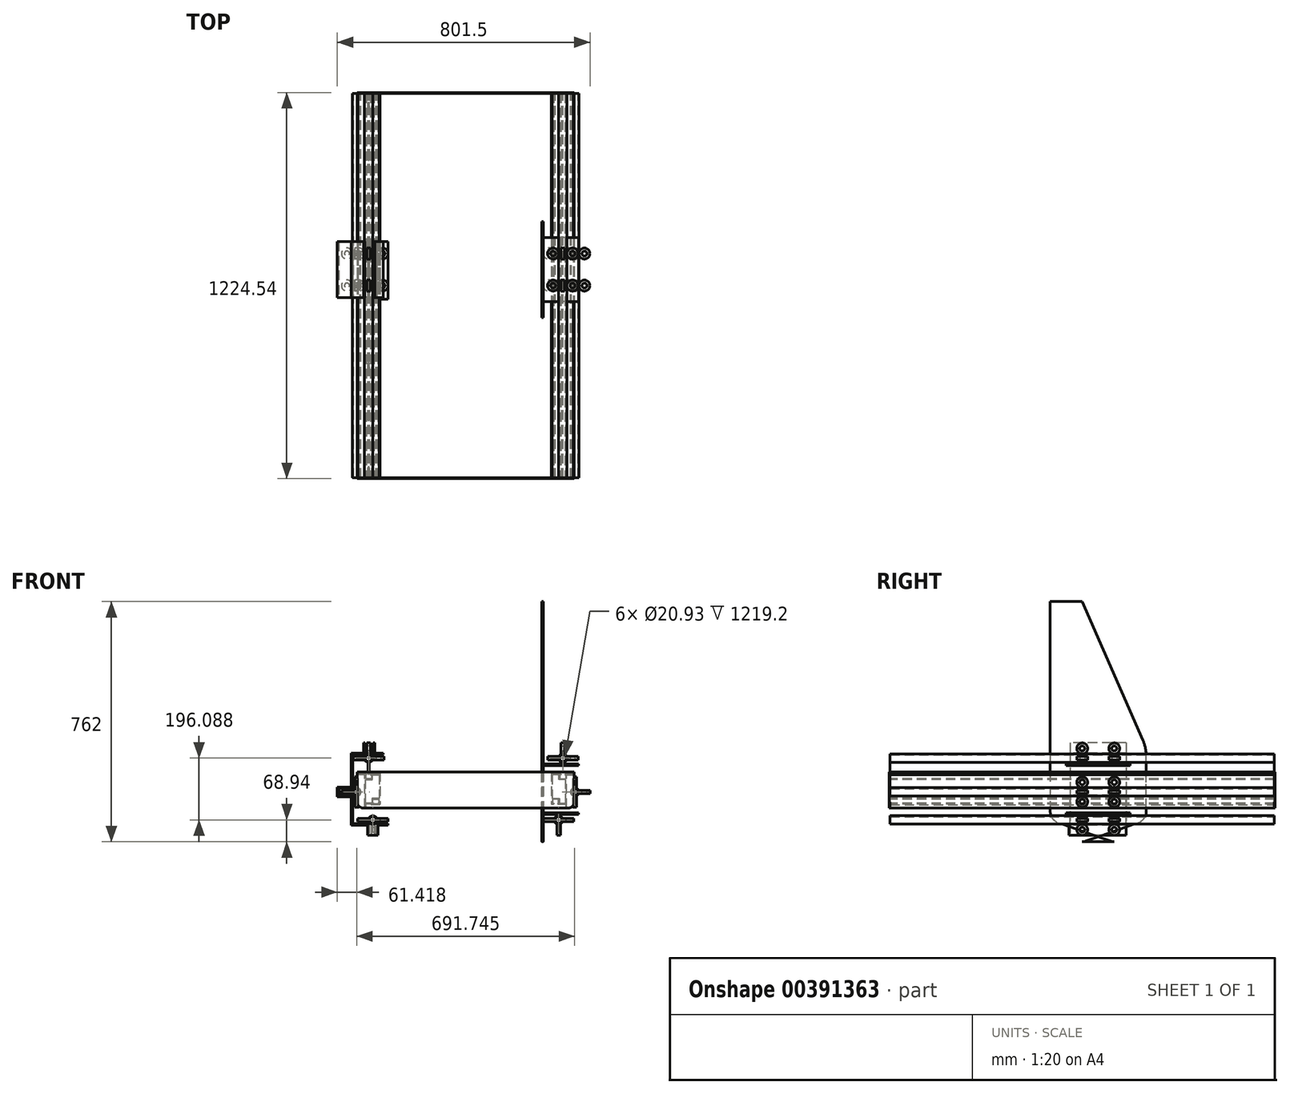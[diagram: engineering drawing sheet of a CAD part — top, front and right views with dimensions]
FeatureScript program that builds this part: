
annotation { "Feature Type Name" : "Feature", "Feature Type Description" : "" }
export const myFeature = defineFeature(function(context is Context, id is Id, definition is map)
    precondition{}
    {
        {
            var Q0;
            Q0=qCreatedBy(makeId("Front.planeOp"),FACE);
            var sketch = newSketch(context, id + "F0", { "sketchPlane" : qUnion([Q0])});
            skPoint(sketch, "E0.0", {"position": v(281.5, 0) * mm});
            skLineSegment(sketch, "E1", {"start": v(317.7, 114.05) * mm, "end": v(317.7, 12.7) * mm});
            skLineSegment(sketch, "E2", {"start": v(317.7, 12.7) * mm, "end": v(310.64, 12.7) * mm});
            skLineSegment(sketch, "E3", {"start": v(271.35, 12.7) * mm, "end": v(271.35, 0) * mm});
            skLineSegment(sketch, "E4", {"start": v(271.35, 0) * mm, "end": v(268.8, 0) * mm});
            skLineSegment(sketch, "E5", {"start": v(268.8, 0) * mm, "end": v(268.8, 104.65) * mm});
            skLineSegment(sketch, "E6", {"start": v(268.8, 104.65) * mm, "end": v(244.68, 104.65) * mm});
            skLineSegment(sketch, "E7", {"start": v(244.68, 104.65) * mm, "end": v(244.68, 114.05) * mm});
            skPoint(sketch, "E8.orphan", {"position": v(268.8, 114.05) * mm});
            skLineSegment(sketch, "E9", {"start": v(294.64, 15.24) * mm, "end": v(294.64, 27.65) * mm});
            skLineSegment(sketch, "E10", {"start": v(294.64, 27.65) * mm, "end": v(313.7, 27.65) * mm});
            skLineSegment(sketch, "E11", {"start": v(313.7, 27.65) * mm, "end": v(313.7, 15.24) * mm});
            skLineSegment(sketch, "E12", {"start": v(317.7, 114.05) * mm, "end": v(315.16, 114.05) * mm});
            skLineSegment(sketch, "E13", {"start": v(315.16, 114.05) * mm, "end": v(315.16, 107.19) * mm});
            skLineSegment(sketch, "E14", {"start": v(315.16, 107.19) * mm, "end": v(290.4, 107.19) * mm});
            skLineSegment(sketch, "E15", {"start": v(290.4, 104.65) * mm, "end": v(290.4, 92.24) * mm});
            skLineSegment(sketch, "E16", {"start": v(290.4, 92.24) * mm, "end": v(271.35, 92.24) * mm});
            skLineSegment(sketch, "E17", {"start": v(244.68, 114.05) * mm, "end": v(247.22, 114.05) * mm});
            skLineSegment(sketch, "E18", {"start": v(247.22, 114.05) * mm, "end": v(247.22, 107.19) * mm});
            skLineSegment(sketch, "E19", {"start": v(247.22, 107.19) * mm, "end": v(271.35, 107.19) * mm});
            skLineSegment(sketch, "E20", {"start": v(271.35, 104.65) * mm, "end": v(271.35, 92.24) * mm});
            skLineSegment(sketch, "E21", {"start": v(290.4, 107.19) * mm, "end": v(287.35, 107.19) * mm});
            skLineSegment(sketch, "E22", {"start": v(287.35, 107.19) * mm, "end": v(287.35, 104.65) * mm});
            skLineSegment(sketch, "E23", {"start": v(287.35, 104.65) * mm, "end": v(290.4, 104.65) * mm});
            skLineSegment(sketch, "E24", {"start": v(271.35, 107.19) * mm, "end": v(274.4, 107.19) * mm});
            skLineSegment(sketch, "E25", {"start": v(274.4, 107.19) * mm, "end": v(274.4, 104.65) * mm});
            skLineSegment(sketch, "E26", {"start": v(274.4, 104.65) * mm, "end": v(271.35, 104.65) * mm});
            skLineSegment(sketch, "E27", {"start": v(313.7, 15.24) * mm, "end": v(310.64, 15.24) * mm});
            skLineSegment(sketch, "E28", {"start": v(310.64, 15.24) * mm, "end": v(310.64, 12.7) * mm});
            skLineSegment(sketch, "E29", {"start": v(294.64, 15.24) * mm, "end": v(297.69, 15.24) * mm});
            skLineSegment(sketch, "E30", {"start": v(297.69, 15.24) * mm, "end": v(297.69, 12.7) * mm});
            skLineSegment(sketch, "E31.trimOffspring", {"start": v(297.69, 12.7) * mm, "end": v(271.35, 12.7) * mm});
            skLineSegment(sketch, "E32", {"start": v(317.7, 63.37) * mm, "end": v(268.8, 63.37) * mm, "construction": true});
            skLineSegment(sketch, "E33", {"start": v(315.16, 104.65) * mm, "end": v(315.16, 30.19) * mm});
            skLineSegment(sketch, "E34", {"start": v(315.16, 30.19) * mm, "end": v(292.1, 30.19) * mm});
            skLineSegment(sketch, "E35", {"start": v(292.1, 30.19) * mm, "end": v(292.1, 15.24) * mm});
            skLineSegment(sketch, "E36", {"start": v(292.1, 15.24) * mm, "end": v(271.35, 15.24) * mm});
            skLineSegment(sketch, "E37", {"start": v(271.35, 15.24) * mm, "end": v(271.35, 89.7) * mm});
            skLineSegment(sketch, "E38", {"start": v(271.35, 89.7) * mm, "end": v(292.94, 89.7) * mm});
            skLineSegment(sketch, "E39", {"start": v(292.94, 89.7) * mm, "end": v(292.94, 104.65) * mm});
            skLineSegment(sketch, "E40", {"start": v(292.94, 104.65) * mm, "end": v(315.16, 104.65) * mm});
            skPoint(sketch, "E41", {"position": v(293.26, 63.37) * mm});
            skPoint(sketch, "E42", {"position": v(304.17, 27.65) * mm});
            skSolve(sketch);
        }
        {
            var Q0;
            Q0 = qSketchRegion(id + "F0", true);
            extrude(context, id + "F1", {"entities" : qUnion([Q0]), "depth" : 1219.2 * mm, "offsetDistance" : 25.4 * mm, "symmetric" : true});
        }
        {
            var Q0;
            Q0=makeQuery(id+"F1.opExtrude","SWEPT_BODY",BODY,{"disambiguationData":[OSD([sQuery(id+"F0.wireOp",EDGE,"E1"),sQuery(id+"F0.wireOp",EDGE,"E2"),sQuery(id+"F0.wireOp",EDGE,"E3"),sQuery(id+"F0.wireOp",EDGE,"E4"),sQuery(id+"F0.wireOp",EDGE,"E5"),sQuery(id+"F0.wireOp",EDGE,"E6"),sQuery(id+"F0.wireOp",EDGE,"E7"),sQuery(id+"F0.wireOp",EDGE,"E9"),sQuery(id+"F0.wireOp",EDGE,"E10"),sQuery(id+"F0.wireOp",EDGE,"E11"),sQuery(id+"F0.wireOp",EDGE,"E12"),sQuery(id+"F0.wireOp",EDGE,"E13"),sQuery(id+"F0.wireOp",EDGE,"E14"),sQuery(id+"F0.wireOp",EDGE,"E15"),sQuery(id+"F0.wireOp",EDGE,"E16"),sQuery(id+"F0.wireOp",EDGE,"E17"),sQuery(id+"F0.wireOp",EDGE,"E18"),sQuery(id+"F0.wireOp",EDGE,"E19"),sQuery(id+"F0.wireOp",EDGE,"E20"),sQuery(id+"F0.wireOp",EDGE,"E21"),sQuery(id+"F0.wireOp",EDGE,"E22"),sQuery(id+"F0.wireOp",EDGE,"E23"),sQuery(id+"F0.wireOp",EDGE,"E24"),sQuery(id+"F0.wireOp",EDGE,"E25"),sQuery(id+"F0.wireOp",EDGE,"E26"),sQuery(id+"F0.wireOp",EDGE,"E27"),sQuery(id+"F0.wireOp",EDGE,"E28"),sQuery(id+"F0.wireOp",EDGE,"E29"),sQuery(id+"F0.wireOp",EDGE,"E30"),sQuery(id+"F0.wireOp",EDGE,"E31.trimOffspring"),sQuery(id+"F0.wireOp",EDGE,"E33"),sQuery(id+"F0.wireOp",EDGE,"E34"),sQuery(id+"F0.wireOp",EDGE,"E35"),sQuery(id+"F0.wireOp",EDGE,"E36"),sQuery(id+"F0.wireOp",EDGE,"E37"),sQuery(id+"F0.wireOp",EDGE,"E38"),sQuery(id+"F0.wireOp",EDGE,"E39"),sQuery(id+"F0.wireOp",EDGE,"E40")])]});
            var Q1;
            Q1=makeQuery(id+"F1.opExtrude","CAP_EDGE",EDGE,{"disambiguationData":[OSD([sQuery(id+"F0.wireOp",EDGE,"E9")])],"isStart":false});
            transform(context, id + "F2", {"entities" : qUnion([Q0]), "transformType" : TransformType.ROTATION, "transformAxis" : qUnion([Q1]), "angle" : 180 * degree, "makeCopy" : false});
        }
        {
            var Q0;
            Q0=makeQuery(id+"F1.opExtrude","SWEPT_BODY",BODY,{"disambiguationData":[OSD([sQuery(id+"F0.wireOp",EDGE,"E1"),sQuery(id+"F0.wireOp",EDGE,"E2"),sQuery(id+"F0.wireOp",EDGE,"E3"),sQuery(id+"F0.wireOp",EDGE,"E4"),sQuery(id+"F0.wireOp",EDGE,"E5"),sQuery(id+"F0.wireOp",EDGE,"E6"),sQuery(id+"F0.wireOp",EDGE,"E7"),sQuery(id+"F0.wireOp",EDGE,"E9"),sQuery(id+"F0.wireOp",EDGE,"E10"),sQuery(id+"F0.wireOp",EDGE,"E11"),sQuery(id+"F0.wireOp",EDGE,"E12"),sQuery(id+"F0.wireOp",EDGE,"E13"),sQuery(id+"F0.wireOp",EDGE,"E14"),sQuery(id+"F0.wireOp",EDGE,"E15"),sQuery(id+"F0.wireOp",EDGE,"E16"),sQuery(id+"F0.wireOp",EDGE,"E17"),sQuery(id+"F0.wireOp",EDGE,"E18"),sQuery(id+"F0.wireOp",EDGE,"E19"),sQuery(id+"F0.wireOp",EDGE,"E20"),sQuery(id+"F0.wireOp",EDGE,"E21"),sQuery(id+"F0.wireOp",EDGE,"E22"),sQuery(id+"F0.wireOp",EDGE,"E23"),sQuery(id+"F0.wireOp",EDGE,"E24"),sQuery(id+"F0.wireOp",EDGE,"E25"),sQuery(id+"F0.wireOp",EDGE,"E26"),sQuery(id+"F0.wireOp",EDGE,"E27"),sQuery(id+"F0.wireOp",EDGE,"E28"),sQuery(id+"F0.wireOp",EDGE,"E29"),sQuery(id+"F0.wireOp",EDGE,"E30"),sQuery(id+"F0.wireOp",EDGE,"E31.trimOffspring"),sQuery(id+"F0.wireOp",EDGE,"E33"),sQuery(id+"F0.wireOp",EDGE,"E34"),sQuery(id+"F0.wireOp",EDGE,"E35"),sQuery(id+"F0.wireOp",EDGE,"E36"),sQuery(id+"F0.wireOp",EDGE,"E37"),sQuery(id+"F0.wireOp",EDGE,"E38"),sQuery(id+"F0.wireOp",EDGE,"E39"),sQuery(id+"F0.wireOp",EDGE,"E40")])]});
            var Q1;
            Q1=qCreatedBy(makeId("Front.planeOp"),FACE);
            transform(context, id + "F3", {"entities" : qUnion([Q0]), "transformType" : TransformType.TRANSLATION_DISTANCE, "transformDirection" : qUnion([Q1]), "distance" : 1219.2 * mm, "oppositeDirection" : true, "makeCopy" : false});
        }
        {
            var Q0;
            Q0=makeQuery(id+"F1.opExtrude","SWEPT_BODY",BODY,{"disambiguationData":[OSD([sQuery(id+"F0.wireOp",EDGE,"E1"),sQuery(id+"F0.wireOp",EDGE,"E2"),sQuery(id+"F0.wireOp",EDGE,"E3"),sQuery(id+"F0.wireOp",EDGE,"E4"),sQuery(id+"F0.wireOp",EDGE,"E5"),sQuery(id+"F0.wireOp",EDGE,"E6"),sQuery(id+"F0.wireOp",EDGE,"E7"),sQuery(id+"F0.wireOp",EDGE,"E9"),sQuery(id+"F0.wireOp",EDGE,"E10"),sQuery(id+"F0.wireOp",EDGE,"E11"),sQuery(id+"F0.wireOp",EDGE,"E12"),sQuery(id+"F0.wireOp",EDGE,"E13"),sQuery(id+"F0.wireOp",EDGE,"E14"),sQuery(id+"F0.wireOp",EDGE,"E15"),sQuery(id+"F0.wireOp",EDGE,"E16"),sQuery(id+"F0.wireOp",EDGE,"E17"),sQuery(id+"F0.wireOp",EDGE,"E18"),sQuery(id+"F0.wireOp",EDGE,"E19"),sQuery(id+"F0.wireOp",EDGE,"E20"),sQuery(id+"F0.wireOp",EDGE,"E21"),sQuery(id+"F0.wireOp",EDGE,"E22"),sQuery(id+"F0.wireOp",EDGE,"E23"),sQuery(id+"F0.wireOp",EDGE,"E24"),sQuery(id+"F0.wireOp",EDGE,"E25"),sQuery(id+"F0.wireOp",EDGE,"E26"),sQuery(id+"F0.wireOp",EDGE,"E27"),sQuery(id+"F0.wireOp",EDGE,"E28"),sQuery(id+"F0.wireOp",EDGE,"E29"),sQuery(id+"F0.wireOp",EDGE,"E30"),sQuery(id+"F0.wireOp",EDGE,"E31.trimOffspring"),sQuery(id+"F0.wireOp",EDGE,"E33"),sQuery(id+"F0.wireOp",EDGE,"E34"),sQuery(id+"F0.wireOp",EDGE,"E35"),sQuery(id+"F0.wireOp",EDGE,"E36"),sQuery(id+"F0.wireOp",EDGE,"E37"),sQuery(id+"F0.wireOp",EDGE,"E38"),sQuery(id+"F0.wireOp",EDGE,"E39"),sQuery(id+"F0.wireOp",EDGE,"E40")])]});
            var Q1;
            Q1=qCreatedBy(makeId("Right.planeOp"),FACE);
            mirror(context, id + "F4", {"entities" : qUnion([Q0]), "mirrorPlane" : qUnion([Q1])});
        }
        {
            var Q0;
            Q0=qCreatedBy(makeId("Front.planeOp"),FACE);
            var sketch = newSketch(context, id + "F5", { "sketchPlane" : qUnion([Q0])});
            skPoint(sketch, "E43", {"position": v(-308.1, 157.99) * mm});
            skPoint(sketch, "E44", {"position": v(-345.87, 50.67) * mm});
            skPoint(sketch, "E45", {"position": v(-294.76, -38.1) * mm});
            skPoint(sketch, "E46.0", {"position": v(-317.93, 12.7) * mm});
            skPoint(sketch, "E46.1", {"position": v(-271.58, 12.7) * mm});
            skPoint(sketch, "E46.2", {"position": v(-342.06, 107.19) * mm});
            skPoint(sketch, "E46.3", {"position": v(-274.12, 107.19) * mm});
            skPoint(sketch, "E46.4", {"position": v(-271.58, 114.05) * mm});
            skLineSegment(sketch, "E47", {"start": v(-271.58, 114.05) * mm, "end": v(-271.58, 12.7) * mm, "construction": true});
            skLineSegment(sketch, "E48", {"start": v(-271.58, 12.7) * mm, "end": v(-317.93, 12.7) * mm, "construction": true});
            skLineSegment(sketch, "E49", {"start": v(-342.06, 107.19) * mm, "end": v(-274.12, 107.19) * mm, "construction": true});
            skPoint(sketch, "E50", {"position": v(-308.1, 107.19) * mm});
            skPoint(sketch, "E51", {"position": v(-294.76, 12.7) * mm});
            skPoint(sketch, "E52", {"position": v(-271.58, 63.37) * mm});
            skCircle(sketch, "E53", {"center": v(-345.87, 50.67) * mm, "radius": 13.34 * mm});
            skCircle(sketch, "E54", {"center": v(-294.76, -38.1) * mm, "radius": 13.34 * mm});
            skCircle(sketch, "E55", {"center": v(-308.1, 157.99) * mm, "radius": 13.34 * mm});
            skCircle(sketch, "E56.0", {"center": v(-308.1, 157.99) * mm, "radius": 10.46 * mm});
            skCircle(sketch, "E57", {"center": v(-345.87, 50.67) * mm, "radius": 10.46 * mm});
            skCircle(sketch, "E58", {"center": v(-294.76, -38.1) * mm, "radius": 10.46 * mm});
            skSolve(sketch);
        }
        {
            var Q0;
            Q0 = qSketchRegion(id + "F5", true);
            extrude(context, id + "F6", {"entities" : qUnion([Q0]), "depth" : 1219.2 * mm, "offsetDistance" : 25.4 * mm, "symmetric" : true});
        }
        {
            var Q0;
            Q0=qCreatedBy(makeId("Front.planeOp"),FACE);
            var sketch = newSketch(context, id + "F7", { "sketchPlane" : qUnion([Q0])});
            skCircle(sketch, "E59.0", {"center": v(-345.87, 50.67) * mm, "radius": 10.46 * mm, "construction": true});
            skCircle(sketch, "E59.1", {"center": v(-308.1, 157.99) * mm, "radius": 10.46 * mm, "construction": true});
            skCircle(sketch, "E59.2", {"center": v(-294.76, -38.1) * mm, "radius": 10.46 * mm, "construction": true});
            skLineSegment(sketch, "E60", {"start": v(-345.87, 81.5) * mm, "end": v(-345.87, 19.84) * mm, "construction": true});
            skLineSegment(sketch, "E61", {"start": v(-345.87, 50.67) * mm, "end": v(-315.04, 50.67) * mm, "construction": true});
            skLineSegment(sketch, "E62", {"start": v(-325.6, -38.1) * mm, "end": v(-263.92, -38.1) * mm, "construction": true});
            skLineSegment(sketch, "E63", {"start": v(-294.76, -38.1) * mm, "end": v(-294.76, -68.94) * mm, "construction": true});
            skLineSegment(sketch, "E64", {"start": v(-277.25, 157.99) * mm, "end": v(-338.93, 157.99) * mm, "construction": true});
            skLineSegment(sketch, "E65", {"start": v(-308.1, 157.99) * mm, "end": v(-308.1, 188.82) * mm, "construction": true});
            skSolve(sketch);
        }
        {
            var Q0;
            Q0=sQuery(id+"F7.wireOp",EDGE,"E64");
            cPlane(context, id + "F8", {"entities" : qUnion([Q0]), "cplaneType" : CPlaneType.LINE_ANGLE, "offset" : 25.4 * mm, "angle" : 90 * degree, "width" : 152.4 * mm, "height" : 152.4 * mm});
        }
        {
            var Q0;
            Q0=sQuery(id+"F7.wireOp",EDGE,"E60");
            cPlane(context, id + "F9", {"entities" : qUnion([Q0]), "cplaneType" : CPlaneType.LINE_ANGLE, "offset" : 25.4 * mm, "angle" : 0 * degree, "width" : 152.4 * mm, "height" : 152.4 * mm});
        }
        {
            var Q0;
            Q0=sQuery(id+"F7.wireOp",EDGE,"E62");
            cPlane(context, id + "F10", {"entities" : qUnion([Q0]), "cplaneType" : CPlaneType.LINE_ANGLE, "offset" : 25.4 * mm, "angle" : 90 * degree, "width" : 152.4 * mm, "height" : 152.4 * mm});
        }
        {
            var Q0;
            Q0=sQuery(id+"F7.wireOp",EDGE,"E63");
            cPlane(context, id + "F11", {"entities" : qUnion([Q0]), "cplaneType" : CPlaneType.LINE_ANGLE, "offset" : 25.4 * mm, "angle" : 0 * degree, "width" : 152.4 * mm, "height" : 152.4 * mm});
        }
        {
            var Q0;
            Q0=sQuery(id+"F7.wireOp",EDGE,"E61");
            cPlane(context, id + "F12", {"entities" : qUnion([Q0]), "cplaneType" : CPlaneType.LINE_ANGLE, "offset" : 25.4 * mm, "angle" : 90 * degree, "width" : 152.4 * mm, "height" : 152.4 * mm});
        }
        {
            var Q0;
            Q0=sQuery(id+"F7.wireOp",EDGE,"E65");
            cPlane(context, id + "F13", {"entities" : qUnion([Q0]), "cplaneType" : CPlaneType.LINE_ANGLE, "offset" : 25.4 * mm, "angle" : 0 * degree, "width" : 152.4 * mm, "height" : 152.4 * mm});
        }
        {
            var Q0;
            Q0=qCreatedBy(id+"F10.planeOp",FACE);
            var sketch = newSketch(context, id + "F14", { "sketchPlane" : qUnion([Q0])});
            skPoint(sketch, "E66.0", {"position": v(-325.6, 0) * mm});
            skPoint(sketch, "E66.1", {"position": v(-263.92, 0) * mm});
            skCircle(sketch, "E67", {"center": v(-325.6, 0) * mm, "radius": 17.5 * mm});
            skCircle(sketch, "E68", {"center": v(-263.92, 0) * mm, "radius": 17.5 * mm});
            skCircle(sketch, "E69", {"center": v(-325.6, 0) * mm, "radius": 7.94 * mm});
            skCircle(sketch, "E70", {"center": v(-263.92, 0) * mm, "radius": 7.94 * mm});
            skSolve(sketch);
        }
        {
            var Q0;
            Q0 = qSketchRegion(id + "F14", true);
            extrude(context, id + "F15", {"entities" : qUnion([Q0]), "depth" : 11 * mm, "offsetDistance" : 25.4 * mm, "symmetric" : true});
        }
        {
            var Q0;
            Q0=qCreatedBy(id+"F11.planeOp",FACE);
            var sketch = newSketch(context, id + "F16", { "sketchPlane" : qUnion([Q0])});
            skPoint(sketch, "E71.0", {"position": v(0, -68.94) * mm});
            skCircle(sketch, "E72", {"center": v(0, -68.94) * mm, "radius": 17.5 * mm});
            skCircle(sketch, "E73", {"center": v(0, -68.94) * mm, "radius": 7.94 * mm});
            skSolve(sketch);
        }
        {
            var Q0;
            Q0 = qSketchRegion(id + "F16", true);
            extrude(context, id + "F17", {"entities" : qUnion([Q0]), "depth" : 11 * mm, "offsetDistance" : 25.4 * mm, "symmetric" : true});
        }
        {
            var Q0;
            Q0=qCreatedBy(id+"F9.planeOp",FACE);
            var sketch = newSketch(context, id + "F18", { "sketchPlane" : qUnion([Q0])});
            skPoint(sketch, "E74.0", {"position": v(0, 81.5) * mm});
            skPoint(sketch, "E74.1", {"position": v(0, 19.84) * mm});
            skCircle(sketch, "E75", {"center": v(0, 81.5) * mm, "radius": 17.5 * mm});
            skCircle(sketch, "E76", {"center": v(0, 81.5) * mm, "radius": 7.94 * mm});
            skCircle(sketch, "E77", {"center": v(0, 19.84) * mm, "radius": 17.5 * mm});
            skCircle(sketch, "E78", {"center": v(0, 19.84) * mm, "radius": 7.94 * mm});
            skSolve(sketch);
        }
        {
            var Q0;
            Q0 = qSketchRegion(id + "F18", true);
            extrude(context, id + "F19", {"entities" : qUnion([Q0]), "depth" : 11 * mm, "offsetDistance" : 25.4 * mm, "symmetric" : true});
        }
        {
            var Q0;
            Q0=qCreatedBy(id+"F12.planeOp",FACE);
            var sketch = newSketch(context, id + "F20", { "sketchPlane" : qUnion([Q0])});
            skCircle(sketch, "E79", {"center": v(-315.04, 0) * mm, "radius": 17.5 * mm});
            skCircle(sketch, "E80", {"center": v(-315.04, 0) * mm, "radius": 7.94 * mm});
            skSolve(sketch);
        }
        {
            var Q0;
            Q0 = qSketchRegion(id + "F20", true);
            extrude(context, id + "F21", {"entities" : qUnion([Q0]), "depth" : 11 * mm, "offsetDistance" : 25.4 * mm, "symmetric" : true});
        }
        {
            var Q0;
            Q0=qCreatedBy(id+"F8.planeOp",FACE);
            var sketch = newSketch(context, id + "F22", { "sketchPlane" : qUnion([Q0])});
            skPoint(sketch, "E81.0", {"position": v(-277.25, 0) * mm});
            skPoint(sketch, "E81.1", {"position": v(-338.93, 0) * mm});
            skCircle(sketch, "E82", {"center": v(-277.25, 0) * mm, "radius": 17.5 * mm});
            skCircle(sketch, "E83", {"center": v(-277.25, 0) * mm, "radius": 7.94 * mm});
            skCircle(sketch, "E84", {"center": v(-338.93, 0) * mm, "radius": 17.5 * mm});
            skCircle(sketch, "E85", {"center": v(-338.93, 0) * mm, "radius": 7.94 * mm});
            skSolve(sketch);
        }
        {
            var Q0;
            Q0 = qSketchRegion(id + "F22", true);
            extrude(context, id + "F23", {"entities" : qUnion([Q0]), "depth" : 11 * mm, "offsetDistance" : 25.4 * mm, "symmetric" : true});
        }
        {
            var Q0;
            Q0=qCreatedBy(id+"F13.planeOp",FACE);
            var sketch = newSketch(context, id + "F24", { "sketchPlane" : qUnion([Q0])});
            skCircle(sketch, "E86", {"center": v(0, 188.82) * mm, "radius": 17.5 * mm});
            skCircle(sketch, "E87", {"center": v(0, 188.82) * mm, "radius": 7.94 * mm});
            skSolve(sketch);
        }
        {
            var Q0;
            Q0 = qSketchRegion(id + "F24", true);
            extrude(context, id + "F25", {"entities" : qUnion([Q0]), "depth" : 11 * mm, "offsetDistance" : 25.4 * mm, "symmetric" : true});
        }
        {
            var Q0;
            Q0=makeQuery(id+"F21.opExtrude","SWEPT_BODY",BODY,{"disambiguationData":[OSD([sQuery(id+"F20.wireOp",EDGE,"E79"),sQuery(id+"F20.wireOp",EDGE,"E80")])]});
            var Q1;
            Q1=makeQuery(id+"F19.opExtrude","SWEPT_BODY",BODY,{"disambiguationData":[OSD([sQuery(id+"F18.wireOp",EDGE,"E75"),sQuery(id+"F18.wireOp",EDGE,"E76")])]});
            var Q2;
            Q2=makeQuery(id+"F19.opExtrude","SWEPT_BODY",BODY,{"disambiguationData":[OSD([sQuery(id+"F18.wireOp",EDGE,"E77"),sQuery(id+"F18.wireOp",EDGE,"E78")])]});
            var Q3;
            Q3=makeQuery(id+"F6.opExtrude","CAP_EDGE",EDGE,{"disambiguationData":[OSD([sQuery(id+"F5.wireOp",EDGE,"E57")])],"isStart":false});
            transform(context, id + "F26", {"entities" : qUnion([Q0, Q1, Q2]), "transformType" : TransformType.ROTATION, "transformAxis" : qUnion([Q3]), "angle" : 180 * degree, "makeCopy" : false});
        }
        {
            var Q0;
            Q0=makeQuery(id+"F6.opExtrude","SWEPT_BODY",BODY,{"disambiguationData":[OSD([sQuery(id+"F5.wireOp",EDGE,"E55"),sQuery(id+"F5.wireOp",EDGE,"E56.0")])]});
            var Q1;
            Q1=makeQuery(id+"F23.opExtrude","SWEPT_BODY",BODY,{"disambiguationData":[OSD([sQuery(id+"F22.wireOp",EDGE,"E82"),sQuery(id+"F22.wireOp",EDGE,"E83")])]});
            var Q2;
            Q2=makeQuery(id+"F25.opExtrude","SWEPT_BODY",BODY,{"disambiguationData":[OSD([sQuery(id+"F24.wireOp",EDGE,"E86"),sQuery(id+"F24.wireOp",EDGE,"E87")])]});
            var Q3;
            Q3=makeQuery(id+"F23.opExtrude","SWEPT_BODY",BODY,{"disambiguationData":[OSD([sQuery(id+"F22.wireOp",EDGE,"E84"),sQuery(id+"F22.wireOp",EDGE,"E85")])]});
            var Q4;
            Q4=makeQuery(id+"F21.opExtrude","SWEPT_BODY",BODY,{"disambiguationData":[OSD([sQuery(id+"F20.wireOp",EDGE,"E79"),sQuery(id+"F20.wireOp",EDGE,"E80")])]});
            var Q5;
            Q5=makeQuery(id+"F19.opExtrude","SWEPT_BODY",BODY,{"disambiguationData":[OSD([sQuery(id+"F18.wireOp",EDGE,"E75"),sQuery(id+"F18.wireOp",EDGE,"E76")])]});
            var Q6;
            Q6=makeQuery(id+"F6.opExtrude","SWEPT_BODY",BODY,{"disambiguationData":[OSD([sQuery(id+"F5.wireOp",EDGE,"E53"),sQuery(id+"F5.wireOp",EDGE,"E57")])]});
            var Q7;
            Q7=makeQuery(id+"F15.opExtrude","SWEPT_BODY",BODY,{"disambiguationData":[OSD([sQuery(id+"F14.wireOp",EDGE,"E67"),sQuery(id+"F14.wireOp",EDGE,"E69")])]});
            var Q8;
            Q8=makeQuery(id+"F15.opExtrude","SWEPT_BODY",BODY,{"disambiguationData":[OSD([sQuery(id+"F14.wireOp",EDGE,"E68"),sQuery(id+"F14.wireOp",EDGE,"E70")])]});
            var Q9;
            Q9=makeQuery(id+"F19.opExtrude","SWEPT_BODY",BODY,{"disambiguationData":[OSD([sQuery(id+"F18.wireOp",EDGE,"E77"),sQuery(id+"F18.wireOp",EDGE,"E78")])]});
            var Q10;
            Q10=makeQuery(id+"F17.opExtrude","SWEPT_BODY",BODY,{"disambiguationData":[OSD([sQuery(id+"F16.wireOp",EDGE,"E72"),sQuery(id+"F16.wireOp",EDGE,"E73")])]});
            var Q11;
            Q11=makeQuery(id+"F6.opExtrude","SWEPT_BODY",BODY,{"disambiguationData":[OSD([sQuery(id+"F5.wireOp",EDGE,"E54"),sQuery(id+"F5.wireOp",EDGE,"E58")])]});
            var Q12;
            Q12=qCreatedBy(makeId("Right.planeOp"),FACE);
            mirror(context, id + "F27", {"entities" : qUnion([Q0, Q1, Q2, Q3, Q4, Q5, Q6, Q7, Q8, Q9, Q10, Q11]), "mirrorPlane" : qUnion([Q12])});
        }
        {
            var Q0;
            Q0=makeQuery(id+"F4.opPattern","COPY",FACE,{"derivedFrom":makeQuery(id+"F1.opExtrude","CAP_FACE",FACE,{"disambiguationData":[OSD([sQuery(id+"F0.wireOp",EDGE,"E1"),sQuery(id+"F0.wireOp",EDGE,"E2"),sQuery(id+"F0.wireOp",EDGE,"E3"),sQuery(id+"F0.wireOp",EDGE,"E4"),sQuery(id+"F0.wireOp",EDGE,"E5"),sQuery(id+"F0.wireOp",EDGE,"E6"),sQuery(id+"F0.wireOp",EDGE,"E7"),sQuery(id+"F0.wireOp",EDGE,"E9"),sQuery(id+"F0.wireOp",EDGE,"E10"),sQuery(id+"F0.wireOp",EDGE,"E11"),sQuery(id+"F0.wireOp",EDGE,"E12"),sQuery(id+"F0.wireOp",EDGE,"E13"),sQuery(id+"F0.wireOp",EDGE,"E14"),sQuery(id+"F0.wireOp",EDGE,"E15"),sQuery(id+"F0.wireOp",EDGE,"E16"),sQuery(id+"F0.wireOp",EDGE,"E17"),sQuery(id+"F0.wireOp",EDGE,"E18"),sQuery(id+"F0.wireOp",EDGE,"E19"),sQuery(id+"F0.wireOp",EDGE,"E20"),sQuery(id+"F0.wireOp",EDGE,"E21"),sQuery(id+"F0.wireOp",EDGE,"E22"),sQuery(id+"F0.wireOp",EDGE,"E23"),sQuery(id+"F0.wireOp",EDGE,"E24"),sQuery(id+"F0.wireOp",EDGE,"E25"),sQuery(id+"F0.wireOp",EDGE,"E26"),sQuery(id+"F0.wireOp",EDGE,"E27"),sQuery(id+"F0.wireOp",EDGE,"E28"),sQuery(id+"F0.wireOp",EDGE,"E29"),sQuery(id+"F0.wireOp",EDGE,"E30"),sQuery(id+"F0.wireOp",EDGE,"E31.trimOffspring"),sQuery(id+"F0.wireOp",EDGE,"E33"),sQuery(id+"F0.wireOp",EDGE,"E34"),sQuery(id+"F0.wireOp",EDGE,"E35"),sQuery(id+"F0.wireOp",EDGE,"E36"),sQuery(id+"F0.wireOp",EDGE,"E37"),sQuery(id+"F0.wireOp",EDGE,"E38"),sQuery(id+"F0.wireOp",EDGE,"E39"),sQuery(id+"F0.wireOp",EDGE,"E40")])],"isStart":false}),"instanceName":"1"});
            var sketch = newSketch(context, id + "F28", { "sketchPlane" : qUnion([Q0])});
            skLineSegment(sketch, "E88.bottom", {"start": v(344.6, 114.05) * mm, "end": v(-344.6, 114.05) * mm});
            skLineSegment(sketch, "E88.top", {"start": v(325.55, 0) * mm, "end": v(-325.55, 0) * mm});
            skLineSegment(sketch, "E88.left", {"start": v(344.6, 114.05) * mm, "end": v(344.6, 19.05) * mm});
            skLineSegment(sketch, "E88.right", {"start": v(-344.6, 114.05) * mm, "end": v(-344.6, 19.05) * mm});
            skPoint(sketch, "E89.visualSharp", {"position": v(344.6, 0) * mm});
            skArc(sketch, "E89.filletArc", {"start": v(325.55, 0) * mm, "mid": v(339.02, 5.58) * mm, "end": v(344.6, 19.05) * mm});
            skPoint(sketch, "E90.visualSharp", {"position": v(-344.6, 0) * mm});
            skArc(sketch, "E90.filletArc", {"start": v(-344.6, 19.05) * mm, "mid": v(-339.02, 5.58) * mm, "end": v(-325.55, 0) * mm});
            skSolve(sketch);
        }
        {
            var Q0;
            Q0 = qSketchRegion(id + "F28", true);
            extrude(context, id + "F29", {"entities" : qUnion([Q0]), "depth" : 2.67 * mm, "offsetDistance" : 25.4 * mm});
        }
        {
            var Q0;
            Q0=makeQuery(id+"F29.opExtrude","SWEPT_BODY",BODY,{"disambiguationData":[OSD([sQuery(id+"F28.wireOp",EDGE,"jPTpQtGP-cdSA-U9tl-EdcJ-eb2z8bK1SM3J.bottom"),sQuery(id+"F28.wireOp",EDGE,"jPTpQtGP-cdSA-U9tl-EdcJ-eb2z8bK1SM3J.top"),sQuery(id+"F28.wireOp",EDGE,"jPTpQtGP-cdSA-U9tl-EdcJ-eb2z8bK1SM3J.left"),sQuery(id+"F28.wireOp",EDGE,"jPTpQtGP-cdSA-U9tl-EdcJ-eb2z8bK1SM3J.right"),sQuery(id+"F28.wireOp",EDGE,"775631f8-775d-494f-ae99-780d62494b7c.filletArc"),sQuery(id+"F28.wireOp",EDGE,"f6839ede-4782-4424-82f1-02aa2c62194e.filletArc")])]});
            var Q1;
            Q1=makeQuery(id+"F29.opExtrude","SWEPT_BODY",BODY,{"disambiguationData":[OSD([sQuery(id+"F28.wireOp",EDGE,"E88.bottom"),sQuery(id+"F28.wireOp",EDGE,"E88.top"),sQuery(id+"F28.wireOp",EDGE,"E88.left"),sQuery(id+"F28.wireOp",EDGE,"E88.right"),sQuery(id+"F28.wireOp",EDGE,"E89.filletArc"),sQuery(id+"F28.wireOp",EDGE,"E90.filletArc")])]});
            var Q2;
            Q2=qCreatedBy(makeId("Front.planeOp"),FACE);
            mirror(context, id + "F30", {"entities" : qUnion([Q0, Q1]), "mirrorPlane" : qUnion([Q2])});
        }
        {
            var Q0;
            Q0=qCreatedBy(makeId("Front.planeOp"),FACE);
            cPlane(context, id + "F31", {"entities" : qUnion([Q0]), "cplaneType" : CPlaneType.OFFSET, "offset" : 50.8 * mm, "oppositeDirection" : true, "width" : 152.4 * mm, "height" : 152.4 * mm});
        }
        {
            var Q0;
            Q0=makeQuery(id+"F27.opPattern","COPY",BODY,{"derivedFrom":makeQuery(id+"F21.opExtrude","SWEPT_BODY",BODY,{"disambiguationData":[OSD([sQuery(id+"F20.wireOp",EDGE,"E79"),sQuery(id+"F20.wireOp",EDGE,"E80")])]}),"instanceName":"1"});
            var Q1;
            Q1=makeQuery(id+"F27.opPattern","COPY",BODY,{"derivedFrom":makeQuery(id+"F19.opExtrude","SWEPT_BODY",BODY,{"disambiguationData":[OSD([sQuery(id+"F18.wireOp",EDGE,"E77"),sQuery(id+"F18.wireOp",EDGE,"E78")])]}),"instanceName":"1"});
            var Q2;
            Q2=makeQuery(id+"F27.opPattern","COPY",BODY,{"derivedFrom":makeQuery(id+"F23.opExtrude","SWEPT_BODY",BODY,{"disambiguationData":[OSD([sQuery(id+"F22.wireOp",EDGE,"E84"),sQuery(id+"F22.wireOp",EDGE,"E85")])]}),"instanceName":"1"});
            var Q3;
            Q3=makeQuery(id+"F27.opPattern","COPY",BODY,{"derivedFrom":makeQuery(id+"F25.opExtrude","SWEPT_BODY",BODY,{"disambiguationData":[OSD([sQuery(id+"F24.wireOp",EDGE,"E86"),sQuery(id+"F24.wireOp",EDGE,"E87")])]}),"instanceName":"1"});
            var Q4;
            Q4=makeQuery(id+"F27.opPattern","COPY",BODY,{"derivedFrom":makeQuery(id+"F23.opExtrude","SWEPT_BODY",BODY,{"disambiguationData":[OSD([sQuery(id+"F22.wireOp",EDGE,"E82"),sQuery(id+"F22.wireOp",EDGE,"E83")])]}),"instanceName":"1"});
            var Q5;
            Q5=makeQuery(id+"F27.opPattern","COPY",BODY,{"derivedFrom":makeQuery(id+"F15.opExtrude","SWEPT_BODY",BODY,{"disambiguationData":[OSD([sQuery(id+"F14.wireOp",EDGE,"E67"),sQuery(id+"F14.wireOp",EDGE,"E69")])]}),"instanceName":"1"});
            var Q6;
            Q6=makeQuery(id+"F27.opPattern","COPY",BODY,{"derivedFrom":makeQuery(id+"F19.opExtrude","SWEPT_BODY",BODY,{"disambiguationData":[OSD([sQuery(id+"F18.wireOp",EDGE,"E75"),sQuery(id+"F18.wireOp",EDGE,"E76")])]}),"instanceName":"1"});
            var Q7;
            Q7=makeQuery(id+"F27.opPattern","COPY",BODY,{"derivedFrom":makeQuery(id+"F15.opExtrude","SWEPT_BODY",BODY,{"disambiguationData":[OSD([sQuery(id+"F14.wireOp",EDGE,"E68"),sQuery(id+"F14.wireOp",EDGE,"E70")])]}),"instanceName":"1"});
            var Q8;
            Q8=makeQuery(id+"F27.opPattern","COPY",BODY,{"derivedFrom":makeQuery(id+"F17.opExtrude","SWEPT_BODY",BODY,{"disambiguationData":[OSD([sQuery(id+"F16.wireOp",EDGE,"E72"),sQuery(id+"F16.wireOp",EDGE,"E73")])]}),"instanceName":"1"});
            var Q9;
            Q9=makeQuery(id+"F17.opExtrude","SWEPT_BODY",BODY,{"disambiguationData":[OSD([sQuery(id+"F16.wireOp",EDGE,"E72"),sQuery(id+"F16.wireOp",EDGE,"E73")])]});
            var Q10;
            Q10=makeQuery(id+"F15.opExtrude","SWEPT_BODY",BODY,{"disambiguationData":[OSD([sQuery(id+"F14.wireOp",EDGE,"E68"),sQuery(id+"F14.wireOp",EDGE,"E70")])]});
            var Q11;
            Q11=makeQuery(id+"F23.opExtrude","SWEPT_BODY",BODY,{"disambiguationData":[OSD([sQuery(id+"F22.wireOp",EDGE,"E82"),sQuery(id+"F22.wireOp",EDGE,"E83")])]});
            var Q12;
            Q12=makeQuery(id+"F25.opExtrude","SWEPT_BODY",BODY,{"disambiguationData":[OSD([sQuery(id+"F24.wireOp",EDGE,"E86"),sQuery(id+"F24.wireOp",EDGE,"E87")])]});
            var Q13;
            Q13=makeQuery(id+"F15.opExtrude","SWEPT_BODY",BODY,{"disambiguationData":[OSD([sQuery(id+"F14.wireOp",EDGE,"E67"),sQuery(id+"F14.wireOp",EDGE,"E69")])]});
            var Q14;
            Q14=makeQuery(id+"F19.opExtrude","SWEPT_BODY",BODY,{"disambiguationData":[OSD([sQuery(id+"F18.wireOp",EDGE,"E75"),sQuery(id+"F18.wireOp",EDGE,"E76")])]});
            var Q15;
            Q15=makeQuery(id+"F21.opExtrude","SWEPT_BODY",BODY,{"disambiguationData":[OSD([sQuery(id+"F20.wireOp",EDGE,"E79"),sQuery(id+"F20.wireOp",EDGE,"E80")])]});
            var Q16;
            Q16=makeQuery(id+"F19.opExtrude","SWEPT_BODY",BODY,{"disambiguationData":[OSD([sQuery(id+"F18.wireOp",EDGE,"E77"),sQuery(id+"F18.wireOp",EDGE,"E78")])]});
            var Q17;
            Q17=makeQuery(id+"F23.opExtrude","SWEPT_BODY",BODY,{"disambiguationData":[OSD([sQuery(id+"F22.wireOp",EDGE,"E84"),sQuery(id+"F22.wireOp",EDGE,"E85")])]});
            var Q18;
            Q18=qCreatedBy(id+"F31.planeOp",FACE);
            mirror(context, id + "F32", {"entities" : qUnion([Q0, Q1, Q2, Q3, Q4, Q5, Q6, Q7, Q8, Q9, Q10, Q11, Q12, Q13, Q14, Q15, Q16, Q17]), "mirrorPlane" : qUnion([Q18])});
        }
        {
            var Q0;
            Q0=makeQuery(id+"F1.opExtrude","SWEPT_FACE",FACE,{"disambiguationData":[OSD([sQuery(id+"F0.wireOp",EDGE,"E1")])]});
            cPlane(context, id + "F33", {"entities" : qUnion([Q0]), "cplaneType" : CPlaneType.OFFSET, "offset" : 25.4 * mm, "width" : 152.4 * mm, "height" : 152.4 * mm});
        }
        {
            var Q0;
            Q0=qCreatedBy(id+"F33.planeOp",FACE);
            var sketch = newSketch(context, id + "F34", { "sketchPlane" : qUnion([Q0])});
            skLineSegment(sketch, "E91", {"start": v(101.6, -38.1) * mm, "end": v(-203.2, -38.1) * mm, "construction": true});
            skLineSegment(sketch, "E92", {"start": v(-203.2, -11.08) * mm, "end": v(-203.2, 163.42) * mm});
            skLineSegment(sketch, "E93", {"start": v(-192.57, 214.27) * mm, "end": v(0, 654.96) * mm});
            skLineSegment(sketch, "E94", {"start": v(101.6, 654.96) * mm, "end": v(101.6, -11.08) * mm});
            skLineSegment(sketch, "E95", {"start": v(76.1, -47.04) * mm, "end": v(-89, -104.9) * mm});
            skLineSegment(sketch, "E96", {"start": v(0, -107.04) * mm, "end": v(-101.6, -107.04) * mm});
            skLineSegment(sketch, "E97", {"start": v(-12.6, -104.9) * mm, "end": v(-177.7, -47.04) * mm});
            skPoint(sketch, "E98", {"position": v(-50.8, -38.1) * mm});
            skPoint(sketch, "E99", {"position": v(-50.8, -107.04) * mm});
            skLineSegment(sketch, "E100", {"start": v(-101.6, 19.84) * mm, "end": v(0, 19.84) * mm, "construction": true});
            skPoint(sketch, "E101", {"position": v(-50.8, 19.84) * mm});
            skLineSegment(sketch, "E102", {"start": v(0, 654.96) * mm, "end": v(101.6, 654.96) * mm});
            skLineSegment(sketch, "E103", {"start": v(-50.8, -32.6) * mm, "end": v(-50.8, -43.6) * mm, "construction": true});
            skPoint(sketch, "E104.visualSharp", {"position": v(101.6, -38.1) * mm});
            skArc(sketch, "E104.filletArc", {"start": v(76.1, -47.04) * mm, "mid": v(94.58, -33.12) * mm, "end": v(101.6, -11.08) * mm});
            skPoint(sketch, "E105.visualSharp", {"position": v(-95.12, -107.04) * mm});
            skArc(sketch, "E105.filletArc", {"start": v(-101.6, -107.04) * mm, "mid": v(-95.2, -106.5) * mm, "end": v(-89, -104.9) * mm});
            skPoint(sketch, "E106.visualSharp", {"position": v(-6.48, -107.04) * mm});
            skArc(sketch, "E106.filletArc", {"start": v(-12.6, -104.9) * mm, "mid": v(-6.4, -106.5) * mm, "end": v(0, -107.04) * mm});
            skPoint(sketch, "E107.visualSharp", {"position": v(-203.2, -38.1) * mm});
            skArc(sketch, "E107.filletArc", {"start": v(-203.2, -11.08) * mm, "mid": v(-196.18, -33.12) * mm, "end": v(-177.7, -47.04) * mm});
            skPoint(sketch, "E108.visualSharp", {"position": v(-203.2, 189.96) * mm});
            skArc(sketch, "E108.filletArc", {"start": v(-192.57, 214.27) * mm, "mid": v(-200.52, 189.4) * mm, "end": v(-203.2, 163.42) * mm});
            skSolve(sketch);
        }
        {
            var Q0;
            Q0 = qSketchRegion(id + "F34", true);
            extrude(context, id + "F35", {"entities" : qUnion([Q0]), "depth" : 4.75 * mm, "offsetDistance" : 25.4 * mm});
        }
        {
            var Q0;
            Q0=makeQuery(id+"F35.opExtrude","CAP_FACE",FACE,{"disambiguationData":[OSD([sQuery(id+"F34.wireOp",EDGE,"E92"),sQuery(id+"F34.wireOp",EDGE,"E93"),sQuery(id+"F34.wireOp",EDGE,"E94"),sQuery(id+"F34.wireOp",EDGE,"E95"),sQuery(id+"F34.wireOp",EDGE,"E97"),sQuery(id+"F34.wireOp",EDGE,"E102"),sQuery(id+"F34.wireOp",EDGE,"E104.filletArc"),sQuery(id+"F34.wireOp",EDGE,"E107.filletArc"),sQuery(id+"F34.wireOp",EDGE,"E108.filletArc")])],"isStart":true});
            var sketch = newSketch(context, id + "F36", { "sketchPlane" : qUnion([Q0])});
            skLineSegment(sketch, "E109", {"start": v(0, 188.82) * mm, "end": v(101.6, 188.82) * mm, "construction": true});
            skPoint(sketch, "E110", {"position": v(50.8, 188.82) * mm});
            skLineSegment(sketch, "E111.bottom", {"start": v(-50.8, 135.04) * mm, "end": v(152.4, 135.04) * mm});
            skLineSegment(sketch, "E111.top", {"start": v(-50.8, 139.79) * mm, "end": v(152.4, 139.79) * mm});
            skLineSegment(sketch, "E111.left", {"start": v(-50.8, 135.04) * mm, "end": v(-50.8, 139.79) * mm});
            skLineSegment(sketch, "E111.right", {"start": v(152.4, 135.04) * mm, "end": v(152.4, 139.79) * mm});
            skPoint(sketch, "E111.middle", {"position": v(50.8, 137.41) * mm});
            skLineSegment(sketch, "E112.bottom", {"start": v(-50.8, -19.9) * mm, "end": v(152.4, -19.9) * mm});
            skLineSegment(sketch, "E112.top", {"start": v(-50.8, -15.15) * mm, "end": v(152.4, -15.15) * mm});
            skLineSegment(sketch, "E112.left", {"start": v(-50.8, -19.9) * mm, "end": v(-50.8, -15.15) * mm});
            skLineSegment(sketch, "E112.right", {"start": v(152.4, -19.9) * mm, "end": v(152.4, -15.15) * mm});
            skPoint(sketch, "E112.middle", {"position": v(50.8, -17.52) * mm});
            skSolve(sketch);
        }
        {
            var Q0;
            Q0 = qSketchRegion(id + "F36", true);
            extrude(context, id + "F37", {"entities" : qUnion([Q0]), "depth" : 111.25 * mm, "offsetDistance" : 25.4 * mm});
        }
        {
            var Q0;
            Q0=qCreatedBy(makeId("Front.planeOp"),FACE);
            var sketch = newSketch(context, id + "F38", { "sketchPlane" : qUnion([Q0])});
            skLineSegment(sketch, "E113.bottom", {"start": v(-293.76, 206.32) * mm, "end": v(-289.01, 206.32) * mm});
            skLineSegment(sketch, "E113.top", {"start": v(-293.76, 174.41) * mm, "end": v(-289.01, 174.41) * mm});
            skLineSegment(sketch, "E113.left", {"start": v(-293.76, 206.32) * mm, "end": v(-293.76, 174.41) * mm});
            skLineSegment(sketch, "E113.right", {"start": v(-289.01, 206.32) * mm, "end": v(-289.01, 174.41) * mm});
            skLineSegment(sketch, "E114.bottom", {"start": v(-293.76, 174.41) * mm, "end": v(-261.87, 174.41) * mm});
            skLineSegment(sketch, "E114.top", {"start": v(-293.76, 169.66) * mm, "end": v(-261.87, 169.66) * mm});
            skLineSegment(sketch, "E114.left", {"start": v(-293.76, 174.41) * mm, "end": v(-293.76, 169.66) * mm});
            skLineSegment(sketch, "E114.right", {"start": v(-261.87, 174.41) * mm, "end": v(-261.87, 169.66) * mm});
            skLineSegment(sketch, "E115.bottom", {"start": v(-319.76, 206.32) * mm, "end": v(-324.51, 206.32) * mm});
            skLineSegment(sketch, "E115.top", {"start": v(-319.76, 174.41) * mm, "end": v(-324.51, 174.41) * mm});
            skLineSegment(sketch, "E115.left", {"start": v(-319.76, 206.32) * mm, "end": v(-319.76, 174.41) * mm});
            skLineSegment(sketch, "E115.right", {"start": v(-324.51, 206.32) * mm, "end": v(-324.51, 174.41) * mm});
            skLineSegment(sketch, "E116.bottom", {"start": v(-319.76, 174.41) * mm, "end": v(-358.37, 174.41) * mm});
            skLineSegment(sketch, "E116.top", {"start": v(-319.76, 169.66) * mm, "end": v(-358.37, 169.66) * mm});
            skLineSegment(sketch, "E116.left", {"start": v(-319.76, 174.41) * mm, "end": v(-319.76, 169.66) * mm});
            skLineSegment(sketch, "E116.right", {"start": v(-358.37, 174.41) * mm, "end": v(-358.37, 169.66) * mm});
            skLineSegment(sketch, "E117.bottom", {"start": v(-363.11, 174.41) * mm, "end": v(-358.37, 174.41) * mm});
            skLineSegment(sketch, "E117.top", {"start": v(-363.11, 66.22) * mm, "end": v(-358.37, 66.22) * mm});
            skLineSegment(sketch, "E117.left", {"start": v(-363.11, 174.41) * mm, "end": v(-363.11, 66.22) * mm});
            skLineSegment(sketch, "E117.right", {"start": v(-358.37, 174.41) * mm, "end": v(-358.37, 66.22) * mm});
            skLineSegment(sketch, "E118.bottom", {"start": v(-358.37, 66.22) * mm, "end": v(-402.54, 66.22) * mm});
            skLineSegment(sketch, "E118.top", {"start": v(-358.37, 61.47) * mm, "end": v(-402.54, 61.47) * mm});
            skLineSegment(sketch, "E118.left", {"start": v(-358.37, 66.22) * mm, "end": v(-358.37, 61.47) * mm});
            skLineSegment(sketch, "E118.right", {"start": v(-402.54, 66.22) * mm, "end": v(-402.54, 61.47) * mm});
            skLineSegment(sketch, "E119.bottom", {"start": v(-402.54, 66.22) * mm, "end": v(-407.29, 66.22) * mm});
            skLineSegment(sketch, "E119.top", {"start": v(-402.54, 35.13) * mm, "end": v(-407.29, 35.13) * mm});
            skLineSegment(sketch, "E119.left", {"start": v(-402.54, 66.22) * mm, "end": v(-402.54, 35.13) * mm});
            skLineSegment(sketch, "E119.right", {"start": v(-407.29, 66.22) * mm, "end": v(-407.29, 35.13) * mm});
            skLineSegment(sketch, "E120.bottom", {"start": v(-402.54, 35.13) * mm, "end": v(-358.37, 35.13) * mm});
            skLineSegment(sketch, "E120.top", {"start": v(-402.54, 39.88) * mm, "end": v(-358.37, 39.88) * mm});
            skLineSegment(sketch, "E120.left", {"start": v(-402.54, 35.13) * mm, "end": v(-402.54, 39.88) * mm});
            skLineSegment(sketch, "E120.right", {"start": v(-358.37, 35.13) * mm, "end": v(-358.37, 39.88) * mm});
            skLineSegment(sketch, "E121.bottom", {"start": v(-358.37, 35.13) * mm, "end": v(-363.11, 35.13) * mm});
            skLineSegment(sketch, "E121.top", {"start": v(-358.37, -54.83) * mm, "end": v(-363.11, -54.83) * mm});
            skLineSegment(sketch, "E121.left", {"start": v(-358.37, 35.13) * mm, "end": v(-358.37, -54.83) * mm});
            skLineSegment(sketch, "E121.right", {"start": v(-363.11, 35.13) * mm, "end": v(-363.11, -54.83) * mm});
            skLineSegment(sketch, "E122.bottom", {"start": v(-358.37, -54.83) * mm, "end": v(-306.11, -54.83) * mm});
            skLineSegment(sketch, "E122.top", {"start": v(-358.37, -50.08) * mm, "end": v(-306.11, -50.08) * mm});
            skLineSegment(sketch, "E122.left", {"start": v(-358.37, -54.83) * mm, "end": v(-358.37, -50.08) * mm});
            skLineSegment(sketch, "E122.right", {"start": v(-306.11, -54.83) * mm, "end": v(-306.11, -50.08) * mm});
            skLineSegment(sketch, "E123.bottom", {"start": v(-306.11, -54.83) * mm, "end": v(-310.86, -54.83) * mm});
            skLineSegment(sketch, "E123.top", {"start": v(-306.11, -86.44) * mm, "end": v(-310.86, -86.44) * mm});
            skLineSegment(sketch, "E123.left", {"start": v(-306.11, -54.83) * mm, "end": v(-306.11, -86.44) * mm});
            skLineSegment(sketch, "E123.right", {"start": v(-310.86, -54.83) * mm, "end": v(-310.86, -86.44) * mm});
            skLineSegment(sketch, "E124.0", {"start": v(-300.26, -86.44) * mm, "end": v(-300.26, -51.44) * mm, "construction": true});
            skLineSegment(sketch, "E125.0", {"start": v(-302.59, 206.32) * mm, "end": v(-302.59, 171.32) * mm, "construction": true});
            skLineSegment(sketch, "E126", {"start": v(-319.76, 169.66) * mm, "end": v(-313.6, 171.32) * mm, "construction": true});
            skLineSegment(sketch, "E127", {"start": v(-319.76, 169.66) * mm, "end": v(-321.43, 163.49) * mm, "construction": true});
            skLineSegment(sketch, "E128.0", {"start": v(-356.43, 163.49) * mm, "end": v(-321.43, 163.49) * mm, "construction": true});
            skLineSegment(sketch, "E129.bottom", {"start": v(-283.4, -86.44) * mm, "end": v(-278.65, -86.44) * mm});
            skLineSegment(sketch, "E129.top", {"start": v(-283.4, -54.83) * mm, "end": v(-278.65, -54.83) * mm});
            skLineSegment(sketch, "E129.left", {"start": v(-283.4, -86.44) * mm, "end": v(-283.4, -54.83) * mm});
            skLineSegment(sketch, "E129.right", {"start": v(-278.65, -86.44) * mm, "end": v(-278.65, -54.83) * mm});
            skLineSegment(sketch, "E130.bottom", {"start": v(-283.4, -54.83) * mm, "end": v(-246.47, -54.83) * mm});
            skLineSegment(sketch, "E130.top", {"start": v(-283.4, -50.08) * mm, "end": v(-246.47, -50.08) * mm});
            skLineSegment(sketch, "E130.left", {"start": v(-283.4, -54.83) * mm, "end": v(-283.4, -50.08) * mm});
            skLineSegment(sketch, "E130.right", {"start": v(-246.47, -54.83) * mm, "end": v(-246.47, -50.08) * mm});
            skSolve(sketch);
        }
        {
            var Q0;
            Q0 = qSketchRegion(id + "F38", true);
            extrude(context, id + "F39", {"entities" : qUnion([Q0]), "oppositeDirection" : true, "depth" : 139.7 * mm, "offsetDistance" : 25.4 * mm, "hasSecondDirection" : true, "secondDirectionOppositeDirection" : false, "secondDirectionDepth" : 38.1 * mm});
        }
        {
            var Q0;
            Q0=makeQuery(id+"F4.opPattern","COPY",FACE,{"derivedFrom":makeQuery(id+"F1.opExtrude","SWEPT_FACE",FACE,{"disambiguationData":[OSD([sQuery(id+"F0.wireOp",EDGE,"E14"),sQuery(id+"F0.wireOp",EDGE,"E21")])]}),"instanceName":"1"});
            var sketch = newSketch(context, id + "F40", { "sketchPlane" : qUnion([Q0])});
            skLineSegment(sketch, "E131.bottom", {"start": v(-280.47, 609.6) * mm, "end": v(-335.71, 609.6) * mm});
            skLineSegment(sketch, "E131.top", {"start": v(-280.47, -609.6) * mm, "end": v(-335.71, -609.6) * mm});
            skLineSegment(sketch, "E131.left", {"start": v(-274.12, 603.25) * mm, "end": v(-274.12, -603.25) * mm});
            skLineSegment(sketch, "E131.right", {"start": v(-342.06, 603.25) * mm, "end": v(-342.06, -603.25) * mm});
            skPoint(sketch, "E132.visualSharp", {"position": v(-274.12, 609.6) * mm});
            skArc(sketch, "E132.filletArc", {"start": v(-274.12, 603.25) * mm, "mid": v(-275.98, 607.74) * mm, "end": v(-280.47, 609.6) * mm});
            skPoint(sketch, "E133.visualSharp", {"position": v(-274.12, -609.6) * mm});
            skArc(sketch, "E133.filletArc", {"start": v(-280.47, -609.6) * mm, "mid": v(-275.98, -607.74) * mm, "end": v(-274.12, -603.25) * mm});
            skPoint(sketch, "E134.visualSharp", {"position": v(-342.06, -609.6) * mm});
            skArc(sketch, "E134.filletArc", {"start": v(-342.06, -603.25) * mm, "mid": v(-340.2, -607.74) * mm, "end": v(-335.71, -609.6) * mm});
            skPoint(sketch, "E135.visualSharp", {"position": v(-342.06, 609.6) * mm});
            skArc(sketch, "E135.filletArc", {"start": v(-335.71, 609.6) * mm, "mid": v(-340.2, 607.74) * mm, "end": v(-342.06, 603.25) * mm});
            skLineSegment(sketch, "E136", {"start": v(-308.1, -590.55) * mm, "end": v(-308.1, -577.85) * mm, "construction": true});
            skPoint(sketch, "E136.startSnap0", {"position": v(-308.1, -609.6) * mm});
            skArc(sketch, "E137.0.startCap", {"start": v(-305.72, -590.55) * mm, "mid": v(-308.1, -592.92) * mm, "end": v(-310.46, -590.55) * mm});
            skArc(sketch, "E137.0.endCap", {"start": v(-310.46, -577.85) * mm, "mid": v(-308.1, -575.48) * mm, "end": v(-305.72, -577.85) * mm});
            skLineSegment(sketch, "E137.0.left", {"start": v(-310.46, -590.55) * mm, "end": v(-310.46, -577.85) * mm});
            skLineSegment(sketch, "E137.0.right", {"start": v(-305.72, -590.55) * mm, "end": v(-305.72, -577.85) * mm});
            skArc(sketch, "E138.0.1.0", {"start": v(-305.72, -425.45) * mm, "mid": v(-308.1, -427.82) * mm, "end": v(-310.46, -425.45) * mm});
            skLineSegment(sketch, "E138.0.1.1", {"start": v(-305.72, -425.45) * mm, "end": v(-305.72, -412.75) * mm});
            skLineSegment(sketch, "E138.0.1.2", {"start": v(-310.46, -425.45) * mm, "end": v(-310.46, -412.75) * mm});
            skArc(sketch, "E138.0.1.3", {"start": v(-310.46, -412.75) * mm, "mid": v(-308.1, -410.38) * mm, "end": v(-305.72, -412.75) * mm});
            skArc(sketch, "E138.0.2.0", {"start": v(-305.72, -260.35) * mm, "mid": v(-308.1, -262.72) * mm, "end": v(-310.46, -260.35) * mm});
            skLineSegment(sketch, "E138.0.2.1", {"start": v(-305.72, -260.35) * mm, "end": v(-305.72, -247.65) * mm});
            skLineSegment(sketch, "E138.0.2.2", {"start": v(-310.46, -260.35) * mm, "end": v(-310.46, -247.65) * mm});
            skArc(sketch, "E138.0.2.3", {"start": v(-310.46, -247.65) * mm, "mid": v(-308.1, -245.28) * mm, "end": v(-305.72, -247.65) * mm});
            skArc(sketch, "E138.0.3.0", {"start": v(-305.72, -95.25) * mm, "mid": v(-308.1, -97.62) * mm, "end": v(-310.46, -95.25) * mm});
            skLineSegment(sketch, "E138.0.3.1", {"start": v(-305.72, -95.25) * mm, "end": v(-305.72, -82.55) * mm});
            skLineSegment(sketch, "E138.0.3.2", {"start": v(-310.46, -95.25) * mm, "end": v(-310.46, -82.55) * mm});
            skArc(sketch, "E138.0.3.3", {"start": v(-310.46, -82.55) * mm, "mid": v(-308.1, -80.18) * mm, "end": v(-305.72, -82.55) * mm});
            skArc(sketch, "E138.0.4.0", {"start": v(-305.72, 69.85) * mm, "mid": v(-308.1, 67.48) * mm, "end": v(-310.46, 69.85) * mm});
            skLineSegment(sketch, "E138.0.4.1", {"start": v(-305.72, 69.85) * mm, "end": v(-305.72, 82.55) * mm});
            skLineSegment(sketch, "E138.0.4.2", {"start": v(-310.46, 69.85) * mm, "end": v(-310.46, 82.55) * mm});
            skArc(sketch, "E138.0.4.3", {"start": v(-310.46, 82.55) * mm, "mid": v(-308.1, 84.92) * mm, "end": v(-305.72, 82.55) * mm});
            skArc(sketch, "E138.0.5.0", {"start": v(-305.72, 234.95) * mm, "mid": v(-308.1, 232.58) * mm, "end": v(-310.46, 234.95) * mm});
            skLineSegment(sketch, "E138.0.5.1", {"start": v(-305.72, 234.95) * mm, "end": v(-305.72, 247.65) * mm});
            skLineSegment(sketch, "E138.0.5.2", {"start": v(-310.46, 234.95) * mm, "end": v(-310.46, 247.65) * mm});
            skArc(sketch, "E138.0.5.3", {"start": v(-310.46, 247.65) * mm, "mid": v(-308.1, 250.02) * mm, "end": v(-305.72, 247.65) * mm});
            skArc(sketch, "E138.0.6.0", {"start": v(-305.72, 400.05) * mm, "mid": v(-308.1, 397.68) * mm, "end": v(-310.46, 400.05) * mm});
            skLineSegment(sketch, "E138.0.6.1", {"start": v(-305.72, 400.05) * mm, "end": v(-305.72, 412.75) * mm});
            skLineSegment(sketch, "E138.0.6.2", {"start": v(-310.46, 400.05) * mm, "end": v(-310.46, 412.75) * mm});
            skArc(sketch, "E138.0.6.3", {"start": v(-310.46, 412.75) * mm, "mid": v(-308.1, 415.12) * mm, "end": v(-305.72, 412.75) * mm});
            skArc(sketch, "E138.0.7.0", {"start": v(-305.72, 565.15) * mm, "mid": v(-308.1, 562.78) * mm, "end": v(-310.46, 565.15) * mm});
            skLineSegment(sketch, "E138.0.7.1", {"start": v(-305.72, 565.15) * mm, "end": v(-305.72, 577.85) * mm});
            skLineSegment(sketch, "E138.0.7.2", {"start": v(-310.46, 565.15) * mm, "end": v(-310.46, 577.85) * mm});
            skArc(sketch, "E138.0.7.3", {"start": v(-310.46, 577.85) * mm, "mid": v(-308.1, 580.22) * mm, "end": v(-305.72, 577.85) * mm});
            skLineSegment(sketch, "E138.direction1", {"start": v(-310.46, -590.55) * mm, "end": v(-285.06, -590.55) * mm, "construction": true});
            skLineSegment(sketch, "E138.direction2", {"start": v(-310.46, -590.55) * mm, "end": v(-310.46, -425.45) * mm, "construction": true});
            skSolve(sketch);
        }
        {
            var Q0;
            Q0 = qSketchRegion(id + "F40", true);
            extrude(context, id + "F41", {"entities" : qUnion([Q0]), "depth" : 3.05 * mm, "offsetDistance" : 25.4 * mm});
        }
        {
            var Q0;
            Q0=makeQuery(id+"F41.opExtrude","SWEPT_FACE",FACE,{"disambiguationData":[OSD([sQuery(id+"F40.wireOp",EDGE,"E137.0.left")])]});
            var sketch = newSketch(context, id + "F42", { "sketchPlane" : qUnion([Q0])});
            skLineSegment(sketch, "E139.bottom", {"start": v(-609.6, 107.19) * mm, "end": v(609.6, 107.19) * mm});
            skLineSegment(sketch, "E139.top", {"start": v(-609.6, 144.1) * mm, "end": v(609.6, 144.1) * mm});
            skLineSegment(sketch, "E139.left", {"start": v(-609.6, 107.19) * mm, "end": v(-609.6, 144.1) * mm});
            skLineSegment(sketch, "E139.right", {"start": v(609.6, 107.19) * mm, "end": v(609.6, 144.1) * mm});
            skSolve(sketch);
        }
        {
            var Q0;
            Q0 = qSketchRegion(id + "F42", true);
            extrude(context, id + "F43", {"entities" : qUnion([Q0]), "depth" : 4.75 * mm, "offsetDistance" : 25.4 * mm});
        }
        {
            var Q0;
            Q0=makeQuery(id+"F4.opPattern","COPY",FACE,{"derivedFrom":makeQuery(id+"F1.opExtrude","SWEPT_FACE",FACE,{"disambiguationData":[OSD([sQuery(id+"F0.wireOp",EDGE,"E31.trimOffspring")])]}),"instanceName":"1"});
            var sketch = newSketch(context, id + "F44", { "sketchPlane" : qUnion([Q0])});
            skLineSegment(sketch, "E140.bottom", {"start": v(-317.93, 609.6) * mm, "end": v(-271.58, 609.6) * mm});
            skLineSegment(sketch, "E140.top", {"start": v(-317.93, -609.6) * mm, "end": v(-271.58, -609.6) * mm});
            skLineSegment(sketch, "E140.left", {"start": v(-317.93, 609.6) * mm, "end": v(-317.93, -609.6) * mm});
            skLineSegment(sketch, "E140.right", {"start": v(-271.58, 609.6) * mm, "end": v(-271.58, -609.6) * mm});
            skSolve(sketch);
        }
        {
            var Q0;
            Q0 = qSketchRegion(id + "F44", true);
            extrude(context, id + "F45", {"entities" : qUnion([Q0]), "depth" : 3.05 * mm, "offsetDistance" : 25.4 * mm});
        }
        {
            var Q0;
            Q0=makeQuery(id+"F39.opExtrude","CAP_FACE",FACE,{"disambiguationData":[OSD([sQuery(id+"F38.wireOp",EDGE,"E115.bottom"),sQuery(id+"F38.wireOp",EDGE,"E115.left"),sQuery(id+"F38.wireOp",EDGE,"E115.right"),sQuery(id+"F38.wireOp",EDGE,"E116.bottom"),sQuery(id+"F38.wireOp",EDGE,"E116.top"),sQuery(id+"F38.wireOp",EDGE,"E116.left"),sQuery(id+"F38.wireOp",EDGE,"E117.bottom"),sQuery(id+"F38.wireOp",EDGE,"E117.left"),sQuery(id+"F38.wireOp",EDGE,"E117.right"),sQuery(id+"F38.wireOp",EDGE,"E118.bottom"),sQuery(id+"F38.wireOp",EDGE,"E118.top"),sQuery(id+"F38.wireOp",EDGE,"E118.left"),sQuery(id+"F38.wireOp",EDGE,"E119.bottom"),sQuery(id+"F38.wireOp",EDGE,"E119.top"),sQuery(id+"F38.wireOp",EDGE,"E119.left"),sQuery(id+"F38.wireOp",EDGE,"E119.right"),sQuery(id+"F38.wireOp",EDGE,"E120.bottom"),sQuery(id+"F38.wireOp",EDGE,"E120.top"),sQuery(id+"F38.wireOp",EDGE,"E120.right"),sQuery(id+"F38.wireOp",EDGE,"E121.top"),sQuery(id+"F38.wireOp",EDGE,"E121.left"),sQuery(id+"F38.wireOp",EDGE,"E121.right"),sQuery(id+"F38.wireOp",EDGE,"E122.bottom"),sQuery(id+"F38.wireOp",EDGE,"E122.top"),sQuery(id+"F38.wireOp",EDGE,"E122.right"),sQuery(id+"F38.wireOp",EDGE,"E123.top"),sQuery(id+"F38.wireOp",EDGE,"E123.left"),sQuery(id+"F38.wireOp",EDGE,"E123.right")])],"isStart":true});
            var sketch = newSketch(context, id + "F46", { "sketchPlane" : qUnion([Q0])});
            skLineSegment(sketch, "E141.bottom", {"start": v(-246.47, -50.08) * mm, "end": v(-288.9, -50.08) * mm});
            skLineSegment(sketch, "E141.top", {"start": v(-278.65, -86.44) * mm, "end": v(-310.86, -86.44) * mm});
            skLineSegment(sketch, "E141.left", {"start": v(-246.47, -50.08) * mm, "end": v(-246.47, -54.83) * mm});
            skLineSegment(sketch, "E141.right", {"start": v(-310.86, -50.08) * mm, "end": v(-310.86, -86.44) * mm});
            skLineSegment(sketch, "E142", {"start": v(-278.65, -86.44) * mm, "end": v(-278.65, -54.83) * mm});
            skLineSegment(sketch, "E143", {"start": v(-278.65, -54.83) * mm, "end": v(-246.47, -54.83) * mm});
            skArc(sketch, "E144", {"start": v(-288.9, -50.08) * mm, "mid": v(-294.76, -51.44) * mm, "end": v(-300.6, -50.08) * mm});
            skLineSegment(sketch, "E145.trimOffspring", {"start": v(-300.6, -50.08) * mm, "end": v(-310.86, -50.08) * mm});
            skSolve(sketch);
        }
        {
            var Q0;
            Q0 = qSketchRegion(id + "F46", true);
            extrude(context, id + "F47", {"entities" : qUnion([Q0]), "operationType" : NewBodyOperationType.ADD, "depth" : 4.75 * mm, "offsetDistance" : 25.4 * mm});
        }
    });
